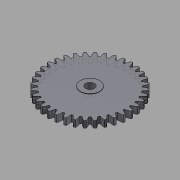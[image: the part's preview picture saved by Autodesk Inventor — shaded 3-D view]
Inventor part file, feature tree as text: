
AUTODESK INVENTOR PART (.ipt)
format: ipt  version: 2015 (Build 190159000, 159)  size: 326,144 bytes
history: native  units: in
note: dims shown in document units (in); Inventor stores cm internally (conversion verified against a paired STEP export)
features: other x13, sketch x4, plane x2
ambient origin geometry x8: Origin, YZ Plane, XZ Plane, XY Plane, X Axis, Y Axis, Z Axis, Center Point
bodies: Solid1 (feature_tree)
feature tree (19):
  other  "Spur Gear27_MIR2.ipt"
  other  "Solid1::Spur Gear27_MIR2.ipt"
  other  "TaggingFeature1"
  sketch  "Sketch1"  dims[d0=0.3937in]
  sketch  "Sketch2"  dims[d16=0.4528in d17=0.0in d41=0.0in d43=0.4528in d46=0.4528in d47=0.0in d48=0.0in]
  sketch  "Sketch3"
  sketch  "Sketch4"
  plane  "XZ Plane_1"
  plane  "Work Plane2"
  other  "Z Axis_1"
  other  "Srf1"
  other  "Srf1::Derived"
  other  "Distance iMate"
  other  "Align iMate"
  other  "Mesh iMate"
  other  "Axis iMate"
  other  "Position iMate"
  other  "Mesh iMate2"
  other  "Start plane iMate"
